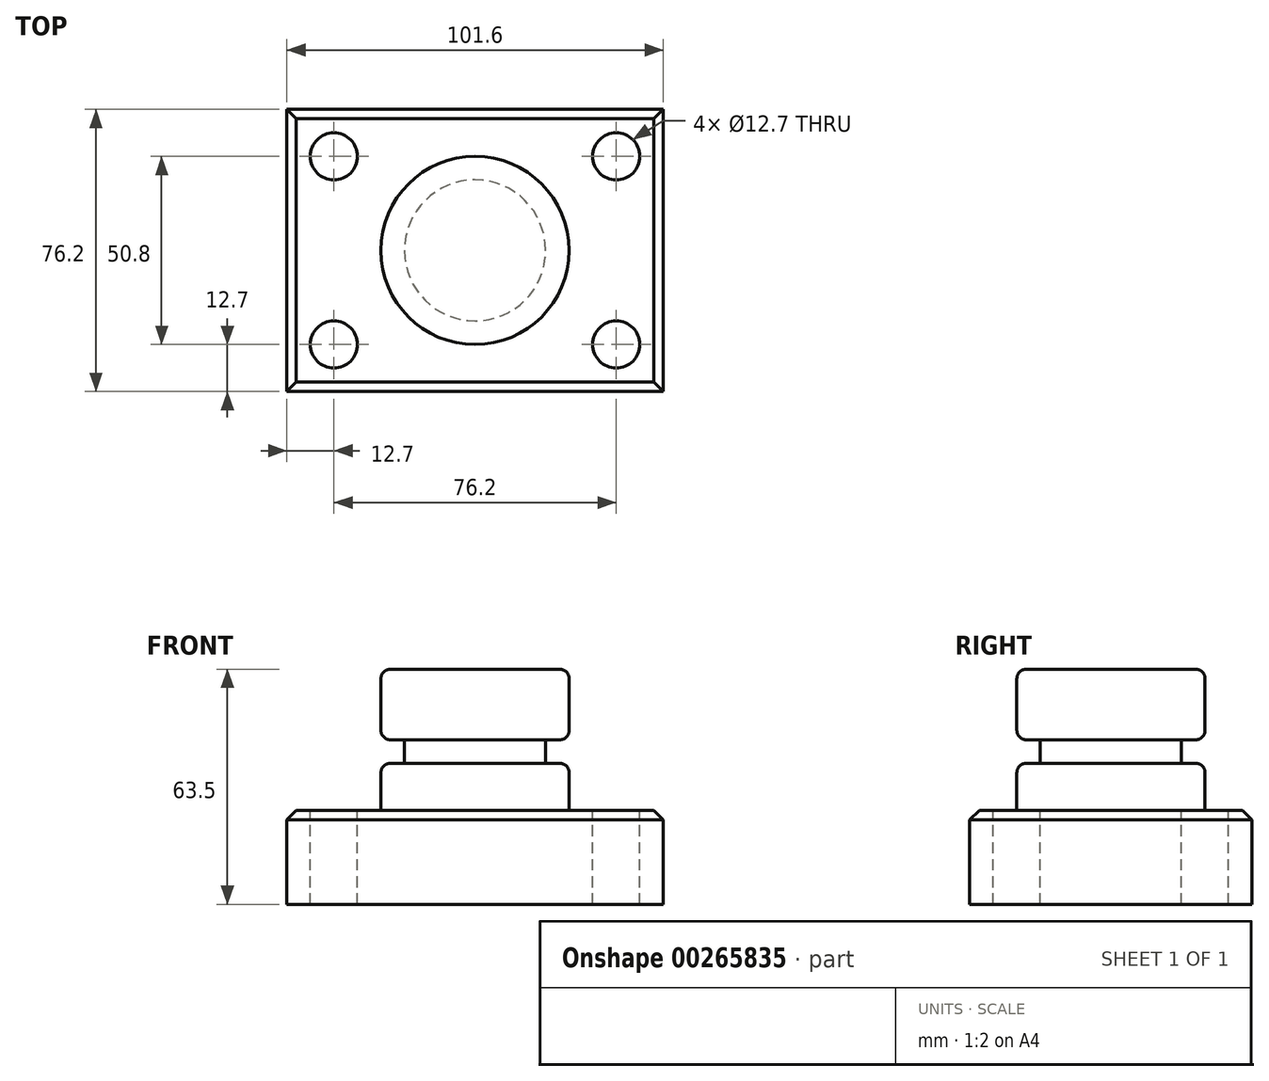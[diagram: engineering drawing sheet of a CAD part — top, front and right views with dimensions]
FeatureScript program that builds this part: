
annotation { "Feature Type Name" : "Feature", "Feature Type Description" : "" }
export const myFeature = defineFeature(function(context is Context, id is Id, definition is map)
    precondition{}
    {
        {
            var Q0;
            Q0=qCreatedBy(makeId("Top.planeOp"),FACE);
            var sketch = newSketch(context, id + "F0", { "sketchPlane" : qUnion([Q0])});
            skLineSegment(sketch, "E0.bottom", {"start": v(-50.8, 38.1) * mm, "end": v(50.8, 38.1) * mm});
            skLineSegment(sketch, "E0.top", {"start": v(-50.8, -38.1) * mm, "end": v(50.8, -38.1) * mm});
            skLineSegment(sketch, "E0.left", {"start": v(-50.8, 38.1) * mm, "end": v(-50.8, -38.1) * mm});
            skLineSegment(sketch, "E0.right", {"start": v(50.8, 38.1) * mm, "end": v(50.8, -38.1) * mm});
            skPoint(sketch, "E0.middle", {"position": v(0, 0) * mm});
            skSolve(sketch);
        }
        {
            var Q0;
            Q0 = qSketchRegion(id + "F0", true);
            extrude(context, id + "F1", {"entities" : qUnion([Q0]), "depth" : 25.4 * mm});
        }
        {
            var Q0;
            Q0=makeQuery(id+"F1.opExtrude","CAP_FACE",FACE,{"disambiguationData":[OSD([sQuery(id+"F0.wireOp",EDGE,"E0.bottom"),sQuery(id+"F0.wireOp",EDGE,"E0.top"),sQuery(id+"F0.wireOp",EDGE,"E0.left"),sQuery(id+"F0.wireOp",EDGE,"E0.right")])],"isStart":false});
            var sketch = newSketch(context, id + "F2", { "sketchPlane" : qUnion([Q0])});
            skCircle(sketch, "E1", {"center": v(-38.1, 25.4) * mm, "radius": 6.35 * mm});
            skCircle(sketch, "E2", {"center": v(38.1, 25.4) * mm, "radius": 6.35 * mm});
            skCircle(sketch, "E3", {"center": v(38.1, -25.4) * mm, "radius": 6.35 * mm});
            skCircle(sketch, "E4", {"center": v(-38.1, -25.4) * mm, "radius": 6.35 * mm});
            skSolve(sketch);
        }
        {
            var Q0;
            Q0 = qSketchRegion(id + "F2", true);
            extrude(context, id + "F3", {"entities" : qUnion([Q0]), "operationType" : NewBodyOperationType.REMOVE, "oppositeDirection" : true, "depth" : 25.4 * mm});
        }
        {
            var Q0;
            Q0=qCreatedBy(makeId("Front.planeOp"),FACE);
            var sketch = newSketch(context, id + "F4", { "sketchPlane" : qUnion([Q0])});
            skLineSegment(sketch, "E5.bottom", {"start": v(-25.4, 63.5) * mm, "end": v(0, 63.5) * mm});
            skLineSegment(sketch, "E5.top", {"start": v(-25.4, 25.4) * mm, "end": v(0, 25.4) * mm});
            skLineSegment(sketch, "E5.left", {"start": v(-25.4, 63.5) * mm, "end": v(-25.4, 25.4) * mm});
            skLineSegment(sketch, "E5.right", {"start": v(0, 63.5) * mm, "end": v(0, 25.4) * mm});
            skSolve(sketch);
        }
        {
            var Q0;
            Q0 = qSketchRegion(id + "F4", true);
            var Q1;
            Q1=sQuery(id+"F4.wireOp",EDGE,"E5.right");
            revolve(context, id + "F5", {"operationType" : NewBodyOperationType.ADD, "entities" : qUnion([Q0]), "axis" : qUnion([Q1]), "revolveType" : RevolveType.FULL});
        }
        {
            var Q0;
            Q0=qCreatedBy(makeId("Right.planeOp"),FACE);
            var sketch = newSketch(context, id + "F6", { "sketchPlane" : qUnion([Q0])});
            skLineSegment(sketch, "E6.bottom", {"start": v(-44.45, 44.45) * mm, "end": v(-19.05, 44.45) * mm});
            skLineSegment(sketch, "E6.top", {"start": v(-44.45, 38.1) * mm, "end": v(-19.05, 38.1) * mm});
            skLineSegment(sketch, "E6.left", {"start": v(-44.45, 44.45) * mm, "end": v(-44.45, 38.1) * mm});
            skLineSegment(sketch, "E6.right", {"start": v(-19.05, 44.45) * mm, "end": v(-19.05, 38.1) * mm});
            skSolve(sketch);
        }
        {
            var Q0;
            Q0 = qSketchRegion(id + "F6", true);
            var Q1;
            Q1=makeQuery(id+"F5.opRevolve","SWEPT_FACE",FACE,{"disambiguationData":[OSD([sQuery(id+"F4.wireOp",EDGE,"E5.left")])]});
            revolve(context, id + "F7", {"operationType" : NewBodyOperationType.REMOVE, "entities" : qUnion([Q0]), "axis" : qUnion([Q1]), "revolveType" : RevolveType.FULL, "oppositeDirection" : true});
        }
        {
            var Q0;
            Q0=makeQuery(id+"F1.opExtrude","CAP_EDGE",EDGE,{"disambiguationData":[OSD([sQuery(id+"F0.wireOp",EDGE,"E0.bottom")])],"isStart":false});
            var Q1;
            Q1=makeQuery(id+"F1.opExtrude","CAP_EDGE",EDGE,{"disambiguationData":[OSD([sQuery(id+"F0.wireOp",EDGE,"E0.left")])],"isStart":false});
            var Q2;
            Q2=makeQuery(id+"F1.opExtrude","CAP_EDGE",EDGE,{"disambiguationData":[OSD([sQuery(id+"F0.wireOp",EDGE,"E0.top")])],"isStart":false});
            var Q3;
            Q3=makeQuery(id+"F1.opExtrude","CAP_EDGE",EDGE,{"disambiguationData":[OSD([sQuery(id+"F0.wireOp",EDGE,"E0.right")])],"isStart":false});
            chamfer(context, id + "F8", {"entities" : qUnion([Q0, Q1, Q2, Q3]), "width" : 2.54 * mm, "tangentPropagation" : true});
        }
        {
            var Q0;
            Q0=makeQuery(id+"F5.opRevolve","SWEPT_EDGE",EDGE,{"disambiguationData":[OSD([sQuery(id+"F4.wireOp",EDGE,"E5.top"),sQuery(id+"F4.wireOp",EDGE,"E5.left")])]});
            var Q1;
            Q1=makeQuery(id+"F7.boolean.opBoolean","INTERSECT",EDGE,{"derivedFrom":[makeQuery(id+"F5.opRevolve","SWEPT_FACE",FACE,{"disambiguationData":[OSD([sQuery(id+"F4.wireOp",EDGE,"E5.left")])]}),makeQuery(id+"F7.opRevolve","SWEPT_FACE",FACE,{"disambiguationData":[OSD([sQuery(id+"F6.wireOp",EDGE,"E6.top")])]})]});
            var Q2;
            Q2=makeQuery(id+"F7.boolean.opBoolean","INTERSECT",EDGE,{"derivedFrom":[makeQuery(id+"F5.opRevolve","SWEPT_FACE",FACE,{"disambiguationData":[OSD([sQuery(id+"F4.wireOp",EDGE,"E5.left")])]}),makeQuery(id+"F7.opRevolve","SWEPT_FACE",FACE,{"disambiguationData":[OSD([sQuery(id+"F6.wireOp",EDGE,"E6.bottom")])]})]});
            var Q3;
            Q3=makeQuery(id+"F5.opRevolve","SWEPT_FACE",FACE,{"disambiguationData":[OSD([sQuery(id+"F4.wireOp",EDGE,"E5.bottom")])]});
            fillet(context, id + "F9", {"entities" : qUnion([Q0, Q1, Q2, Q3]), "radius" : 2.54 * mm, "tangentPropagation" : true, "allowEdgeOverflow" : false});
        }
    });
